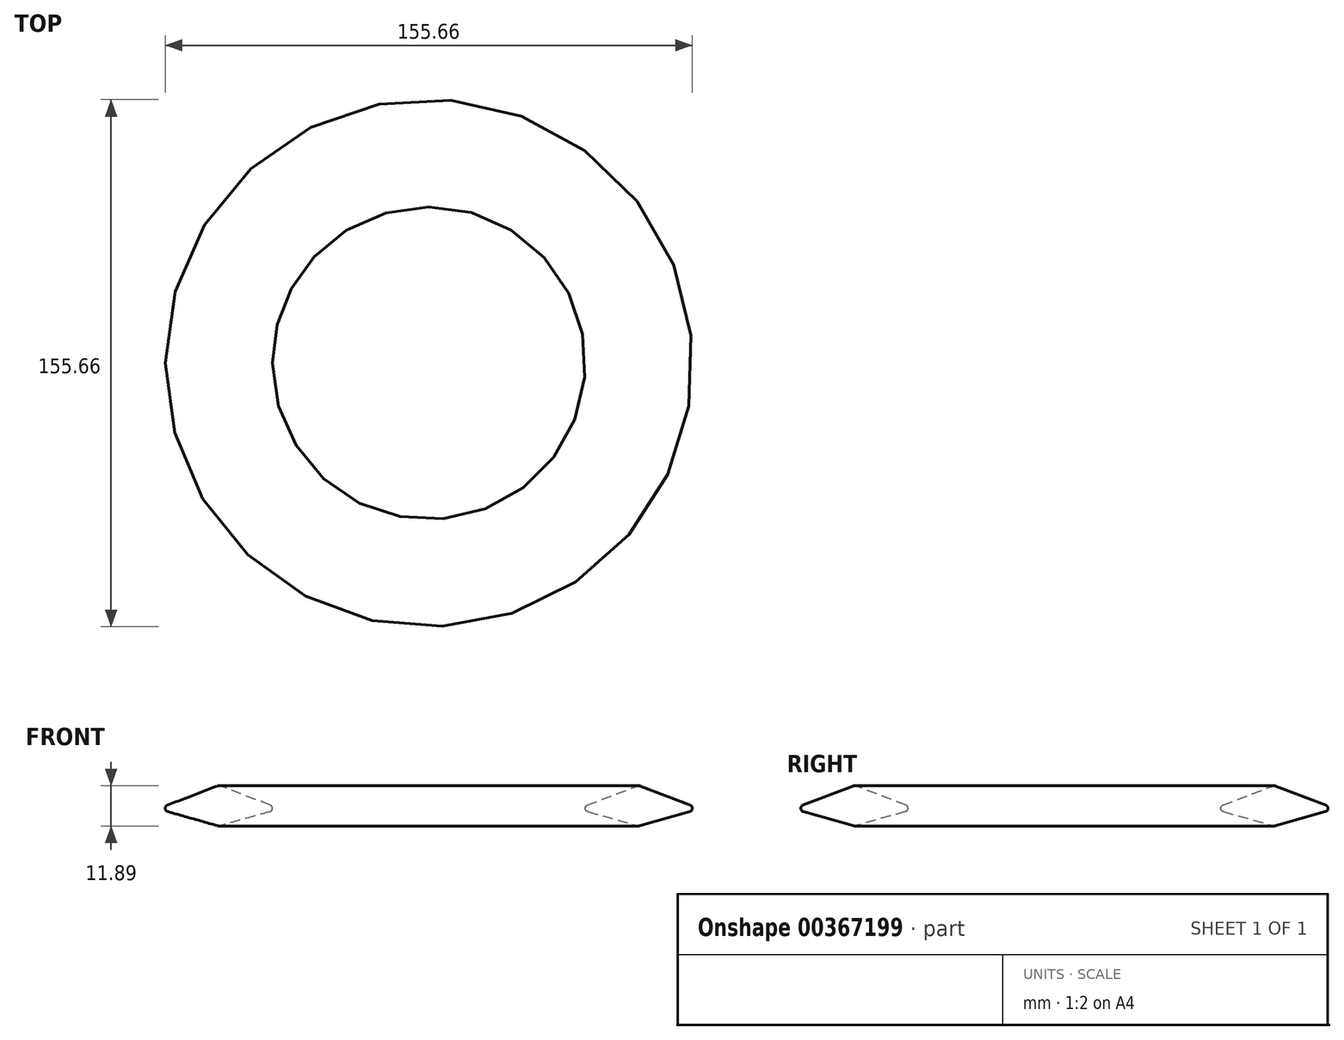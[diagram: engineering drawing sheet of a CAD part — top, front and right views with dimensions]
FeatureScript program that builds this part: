
annotation { "Feature Type Name" : "Feature", "Feature Type Description" : "" }
export const myFeature = defineFeature(function(context is Context, id is Id, definition is map)
    precondition{}
    {
        {
            var Q0;
            Q0=qCreatedBy(makeId("Front.planeOp"),FACE);
            var sketch = newSketch(context, id + "F0", { "sketchPlane" : qUnion([Q0])});
            skLineSegment(sketch, "E0", {"start": v(0, 0) * mm, "end": v(80, 0) * mm, "construction": true});
            skLineSegment(sketch, "E1", {"start": v(80, 0) * mm, "end": v(80, 5.1) * mm, "construction": true});
            skLineSegment(sketch, "E2", {"start": v(0, 0) * mm, "end": v(0, 26.14) * mm, "construction": true});
            skLineSegment(sketch, "E3", {"start": v(77.1, 4.29) * mm, "end": v(62.27, 0.08) * mm});
            skLineSegment(sketch, "E4", {"start": v(61.73, 0.08) * mm, "end": v(46.9, 4.29) * mm});
            skLineSegment(sketch, "E5", {"start": v(46.8, 6.18) * mm, "end": v(61.64, 11.86) * mm});
            skLineSegment(sketch, "E6", {"start": v(62.36, 11.86) * mm, "end": v(77.2, 6.18) * mm});
            skLineSegment(sketch, "E7", {"start": v(62, 0) * mm, "end": v(62, 12) * mm, "construction": true});
            skLineSegment(sketch, "E8", {"start": v(44, 5.1) * mm, "end": v(80, 5.1) * mm, "construction": true});
            skPoint(sketch, "E9.visualSharp", {"position": v(62, 12) * mm});
            skArc(sketch, "E9.filletArc", {"start": v(62.36, 11.86) * mm, "mid": v(62, 11.93) * mm, "end": v(61.64, 11.86) * mm});
            skPoint(sketch, "E10.visualSharp", {"position": v(44, 5.1) * mm});
            skArc(sketch, "E10.filletArc", {"start": v(46.8, 6.18) * mm, "mid": v(46.17, 5.2) * mm, "end": v(46.9, 4.29) * mm});
            skPoint(sketch, "E11.visualSharp", {"position": v(62, 0) * mm});
            skArc(sketch, "E11.filletArc", {"start": v(61.73, 0.08) * mm, "mid": v(62, 0.04) * mm, "end": v(62.27, 0.08) * mm});
            skPoint(sketch, "E12.visualSharp", {"position": v(80, 5.1) * mm});
            skArc(sketch, "E12.filletArc", {"start": v(77.1, 4.29) * mm, "mid": v(77.83, 5.2) * mm, "end": v(77.2, 6.18) * mm});
            skSolve(sketch);
        }
        {
            var Q0;
            Q0=makeQuery(id+"F0.imprint","IMPRINT",FACE,{"disambiguationData":[TD([[makeQuery(id+"F0.imprint","IMPRINT",EDGE,{"derivedFrom":sQuery(id+"F0.wireOp",EDGE,"E3")}),-1.0]])]});
            var Q1;
            Q1=sQuery(id+"F0.wireOp",EDGE,"E2");
            revolve(context, id + "F1", {"entities" : qUnion([Q0]), "axis" : qUnion([Q1]), "revolveType" : RevolveType.FULL});
        }
    });
